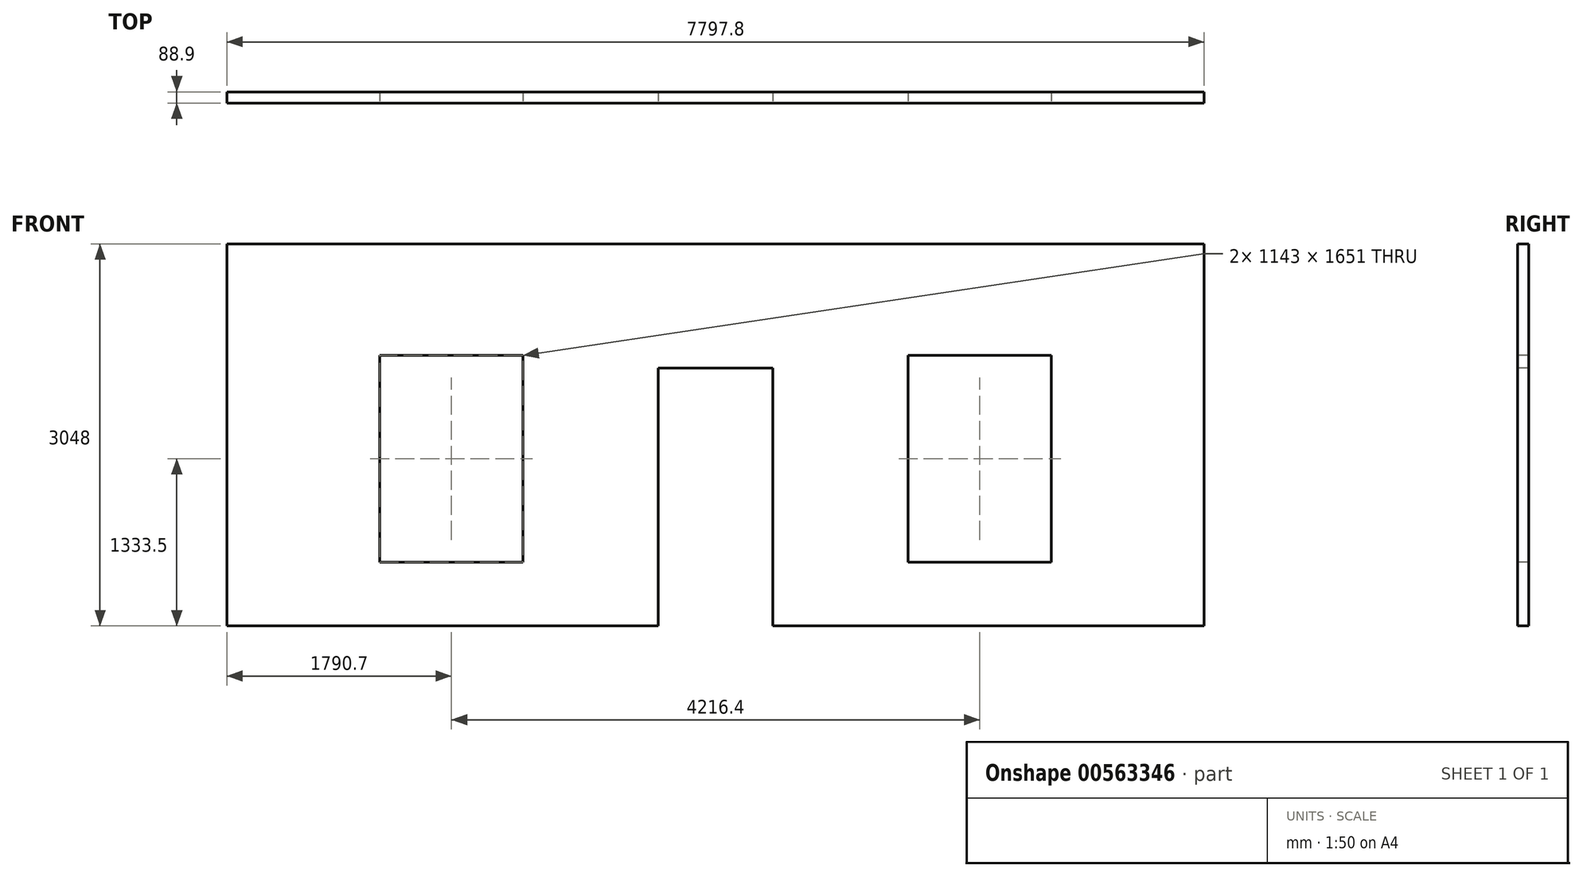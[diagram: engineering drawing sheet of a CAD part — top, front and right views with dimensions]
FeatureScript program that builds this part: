
annotation { "Feature Type Name" : "Feature", "Feature Type Description" : "" }
export const myFeature = defineFeature(function(context is Context, id is Id, definition is map)
    precondition{}
    {
        {
            var Q0;
            Q0=qCreatedBy(makeId("Top.planeOp"),FACE);
            var sketch = newSketch(context, id + "F0", { "sketchPlane" : qUnion([Q0])});
            skLineSegment(sketch, "E0.bottom", {"start": v(3898.9, -44.45) * mm, "end": v(-3898.9, -44.45) * mm});
            skLineSegment(sketch, "E0.top", {"start": v(3898.9, 44.45) * mm, "end": v(-3898.9, 44.45) * mm});
            skLineSegment(sketch, "E0.left", {"start": v(3898.9, -44.45) * mm, "end": v(3898.9, 44.45) * mm});
            skLineSegment(sketch, "E0.right", {"start": v(-3898.9, -44.45) * mm, "end": v(-3898.9, 44.45) * mm});
            skPoint(sketch, "E0.middle", {"position": v(0, 0) * mm});
            skSolve(sketch);
        }
        {
            var Q0;
            Q0 = qSketchRegion(id + "F0", true);
            extrude(context, id + "F1", {"entities" : qUnion([Q0]), "depth" : 3048 * mm, "offsetDistance" : 25.4 * mm});
        }
        {
            var Q0;
            Q0=makeQuery(id+"F1.opExtrude","SWEPT_FACE",FACE,{"disambiguationData":[OSD([sQuery(id+"F0.wireOp",EDGE,"E0.bottom")])]});
            var sketch = newSketch(context, id + "F2", { "sketchPlane" : qUnion([Q0])});
            skLineSegment(sketch, "E1", {"start": v(-2679.7, 2159) * mm, "end": v(-1536.7, 2159) * mm});
            skLineSegment(sketch, "E2", {"start": v(-1536.7, 2159) * mm, "end": v(-1536.7, 508) * mm});
            skLineSegment(sketch, "E3", {"start": v(-1536.7, 508) * mm, "end": v(-2679.7, 508) * mm});
            skLineSegment(sketch, "E4", {"start": v(-2679.7, 508) * mm, "end": v(-2679.7, 2159) * mm});
            skLineSegment(sketch, "E5", {"start": v(0, 0) * mm, "end": v(0, 3048) * mm, "construction": true});
            skLineSegment(sketch, "E6", {"start": v(-457.2, 2057.4) * mm, "end": v(457.2, 2057.4) * mm});
            skLineSegment(sketch, "E7", {"start": v(457.2, 2057.4) * mm, "end": v(457.2, 0) * mm});
            skLineSegment(sketch, "E8", {"start": v(-457.2, 2057.4) * mm, "end": v(-457.2, 0) * mm});
            skLineSegment(sketch, "E9", {"start": v(1536.7, 2159) * mm, "end": v(1536.7, 508) * mm});
            skLineSegment(sketch, "E10", {"start": v(1536.7, 508) * mm, "end": v(2679.7, 508) * mm});
            skLineSegment(sketch, "E11", {"start": v(2679.7, 508) * mm, "end": v(2679.7, 2159) * mm});
            skLineSegment(sketch, "E12", {"start": v(2679.7, 2159) * mm, "end": v(1536.7, 2159) * mm});
            skLineSegment(sketch, "E13", {"start": v(-2108.2, 2159) * mm, "end": v(-2108.2, 508) * mm, "construction": true});
            skLineSegment(sketch, "E14", {"start": v(2108.2, 2159) * mm, "end": v(2108.2, 508) * mm, "construction": true});
            skSolve(sketch);
        }
        {
            var Q0;
            Q0 = qSketchRegion(id + "F2", true);
            var Q1;
            Q1=makeQuery(id+"F2.imprint","IMPRINT",FACE,{"disambiguationData":[TD([[makeQuery(id+"F2.imprint","IMPRINT",EDGE,{"derivedFrom":sQuery(id+"F2.wireOp",EDGE,"E6")}),-1.0]])]});
            extrude(context, id + "F3", {"entities" : qUnion([Q0, Q1]), "operationType" : NewBodyOperationType.REMOVE, "endBound" : BoundingType.THROUGH_ALL, "oppositeDirection" : true, "depth" : 25.4 * mm, "offsetDistance" : 25.4 * mm});
        }
    });
